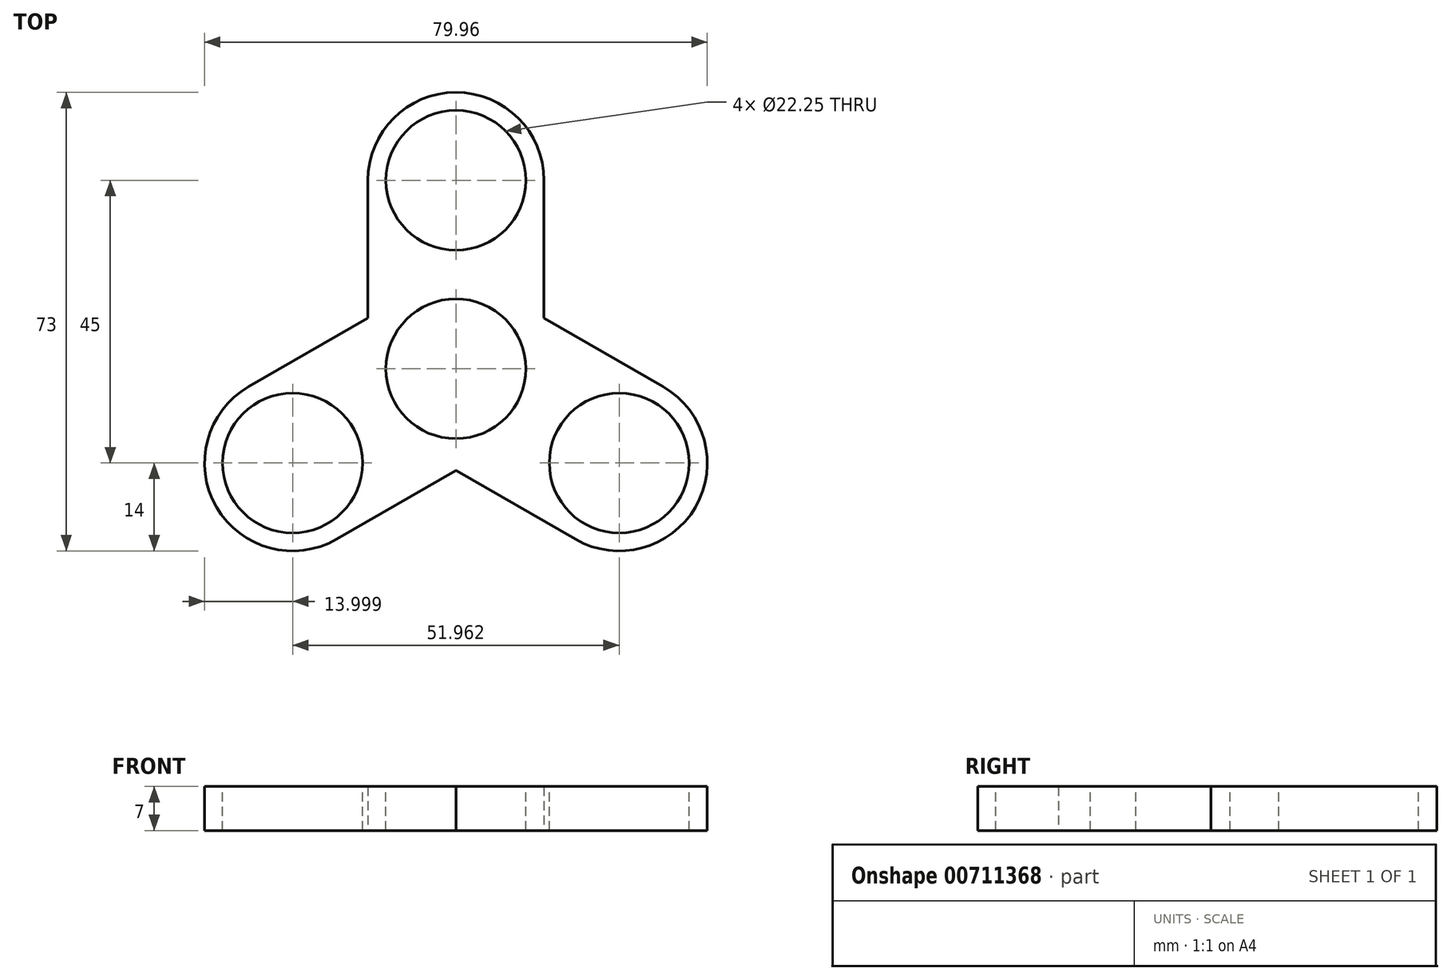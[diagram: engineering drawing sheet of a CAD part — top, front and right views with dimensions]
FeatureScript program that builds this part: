
annotation { "Feature Type Name" : "Feature", "Feature Type Description" : "" }
export const myFeature = defineFeature(function(context is Context, id is Id, definition is map)
    precondition{}
    {
        {
            var Q0;
            Q0=qCreatedBy(makeId("Top.planeOp"),FACE);
            var sketch = newSketch(context, id + "F0", { "sketchPlane" : qUnion([Q0])});
            skCircle(sketch, "E0", {"center": v(0, 0) * mm, "radius": 9.12 * mm});
            skLineSegment(sketch, "E1", {"start": v(0, 0) * mm, "end": v(25.98, -15) * mm, "construction": true});
            skLineSegment(sketch, "E2", {"start": v(0, 0) * mm, "end": v(-25.98, -15) * mm, "construction": true});
            skLineSegment(sketch, "E3", {"start": v(0, 0) * mm, "end": v(0, 30) * mm, "construction": true});
            skCircle(sketch, "E4", {"center": v(0, 30) * mm, "radius": 9.12 * mm});
            skCircle(sketch, "E5", {"center": v(25.98, -15) * mm, "radius": 9.12 * mm});
            skCircle(sketch, "E6", {"center": v(-25.98, -15) * mm, "radius": 9.12 * mm});
            skLineSegment(sketch, "E7", {"start": v(-14, 30) * mm, "end": v(14, 30) * mm, "construction": true});
            skArc(sketch, "E8", {"start": v(-14, 30) * mm, "mid": v(0, 44) * mm, "end": v(14, 30) * mm});
            skCircle(sketch, "E9", {"center": v(0, 0) * mm, "radius": 16.17 * mm, "construction": true});
            skLineSegment(sketch, "E10", {"start": v(-14, 30) * mm, "end": v(-14, 8.08) * mm});
            skLineSegment(sketch, "E11", {"start": v(-32.98, -2.88) * mm, "end": v(-18.98, -27.12) * mm, "construction": true});
            skArc(sketch, "E12", {"start": v(-32.98, -2.88) * mm, "mid": v(-38.1, -22) * mm, "end": v(-18.98, -27.12) * mm});
            skLineSegment(sketch, "E13", {"start": v(-14, 8.08) * mm, "end": v(-32.98, -2.88) * mm});
            skPoint(sketch, "E14.center", {"position": v(0.05, -0.09) * mm});
            skLineSegment(sketch, "E15", {"start": v(32.98, -2.88) * mm, "end": v(18.98, -27.12) * mm, "construction": true});
            skLineSegment(sketch, "E16", {"start": v(-18.98, -27.12) * mm, "end": v(0, -16.17) * mm});
            skLineSegment(sketch, "E17", {"start": v(0, -16.17) * mm, "end": v(18.98, -27.12) * mm});
            skLineSegment(sketch, "E18", {"start": v(14, 30) * mm, "end": v(14, 8.08) * mm});
            skLineSegment(sketch, "E19", {"start": v(14, 8.08) * mm, "end": v(32.98, -2.88) * mm});
            skLineSegment(sketch, "E20", {"start": v(14, 8.08) * mm, "end": v(-14, 8.08) * mm, "construction": true});
            skLineSegment(sketch, "E21", {"start": v(-14, 8.08) * mm, "end": v(0, -16.17) * mm, "construction": true});
            skLineSegment(sketch, "E22", {"start": v(0, -16.17) * mm, "end": v(14, 8.08) * mm, "construction": true});
            skArc(sketch, "E23", {"start": v(18.98, -27.12) * mm, "mid": v(38.1, -22) * mm, "end": v(32.98, -2.88) * mm});
            skSolve(sketch);
        }
        {
            var Q0;
            Q0 = qSketchRegion(id + "F0", true);
            extrude(context, id + "F1", {"entities" : qUnion([Q0]), "depth" : 7 * mm, "offsetDistance" : 25.4 * mm});
        }
        {
            var Q0;
            Q0=makeQuery(id+"F1.opExtrude","CAP_FACE",FACE,{"disambiguationData":[OSD([sQuery(id+"F0.wireOp",EDGE,"E0"),sQuery(id+"F0.wireOp",EDGE,"E4"),sQuery(id+"F0.wireOp",EDGE,"E5"),sQuery(id+"F0.wireOp",EDGE,"E6"),sQuery(id+"F0.wireOp",EDGE,"E8"),sQuery(id+"F0.wireOp",EDGE,"E10"),sQuery(id+"F0.wireOp",EDGE,"E12"),sQuery(id+"F0.wireOp",EDGE,"E13"),sQuery(id+"F0.wireOp",EDGE,"E16"),sQuery(id+"F0.wireOp",EDGE,"E17"),sQuery(id+"F0.wireOp",EDGE,"E18"),sQuery(id+"F0.wireOp",EDGE,"E19"),sQuery(id+"F0.wireOp",EDGE,"E23")])],"isStart":false});
            var sketch = newSketch(context, id + "F2", { "sketchPlane" : qUnion([Q0])});
            skCircle(sketch, "E24", {"center": v(0, 30) * mm, "radius": 11.12 * mm});
            skCircle(sketch, "E25", {"center": v(25.98, -15) * mm, "radius": 11.12 * mm});
            skCircle(sketch, "E26", {"center": v(-25.98, -15) * mm, "radius": 11.12 * mm});
            skCircle(sketch, "E27", {"center": v(0, 0) * mm, "radius": 11.12 * mm});
            skSolve(sketch);
        }
        {
            var Q0;
            Q0 = qSketchRegion(id + "F2", true);
            extrude(context, id + "F3", {"entities" : qUnion([Q0]), "operationType" : NewBodyOperationType.REMOVE, "oppositeDirection" : true, "depth" : 7 * mm, "offsetDistance" : 25 * mm});
        }
    });
